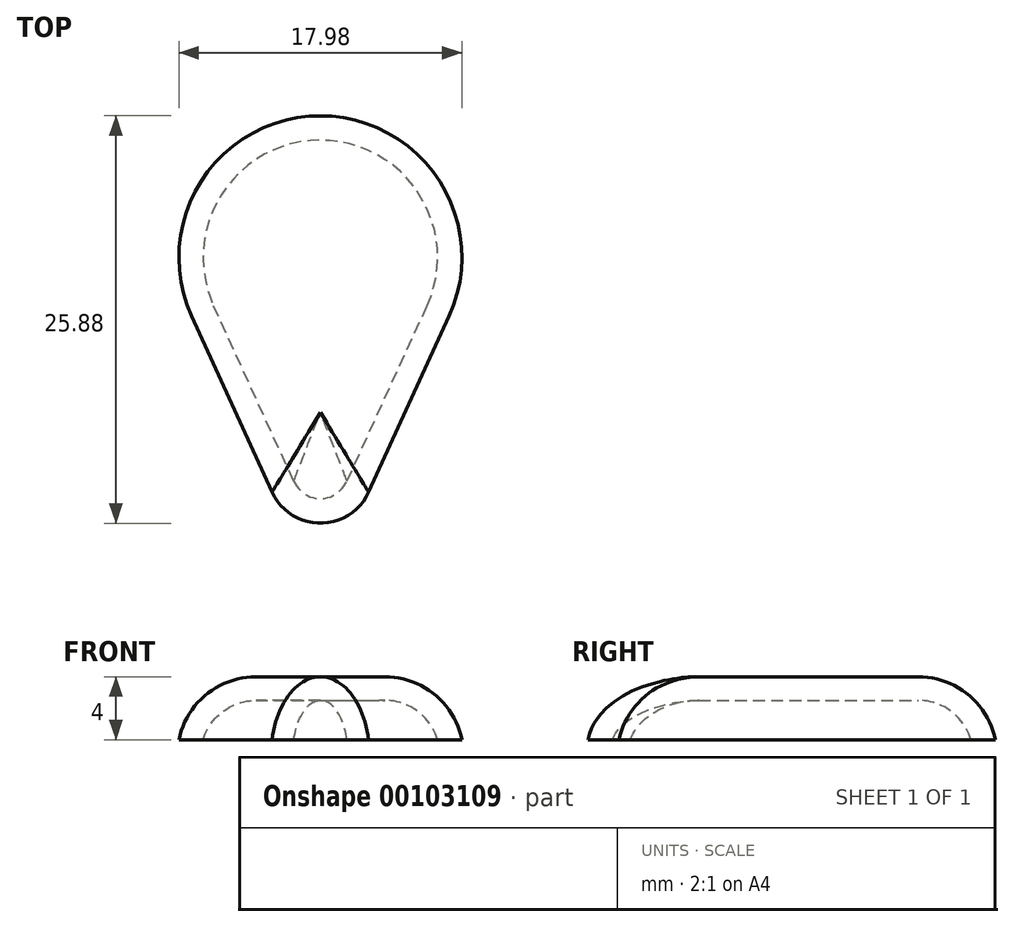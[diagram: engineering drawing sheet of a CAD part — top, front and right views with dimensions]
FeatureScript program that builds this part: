
annotation { "Feature Type Name" : "Feature", "Feature Type Description" : "" }
export const myFeature = defineFeature(function(context is Context, id is Id, definition is map)
    precondition{}
    {
        {
            var Q0;
            Q0=qCreatedBy(makeId("Top.planeOp"),FACE);
            var sketch = newSketch(context, id + "F0", { "sketchPlane" : qUnion([Q0])});
            skLineSegment(sketch, "E0", {"start": v(-3.07, -8.68) * mm, "end": v(-8.18, 2.5) * mm});
            skLineSegment(sketch, "E1.MirrorCS", {"start": v(3.07, -8.68) * mm, "end": v(8.18, 2.5) * mm});
            skArc(sketch, "E2", {"start": v(-3.07, -8.68) * mm, "mid": v(0, -10.65) * mm, "end": v(3.07, -8.68) * mm});
            skArc(sketch, "E3", {"start": v(8.18, 2.5) * mm, "mid": v(0, 15.23) * mm, "end": v(-8.18, 2.5) * mm});
            skSolve(sketch);
        }
        {
            var Q0;
            Q0=makeQuery(id+"F0.imprint","IMPRINT",FACE,{"disambiguationData":[TD([[makeQuery(id+"F0.imprint","IMPRINT",EDGE,{"derivedFrom":sQuery(id+"F0.wireOp",EDGE,"E0")}),-1.0]])]});
            extrude(context, id + "F1", {"entities" : qUnion([Q0]), "depth" : 4 * mm});
        }
        {
            var Q0;
            Q0=makeQuery(id+"F1.opExtrude","CAP_EDGE",EDGE,{"disambiguationData":[OSD([sQuery(id+"F0.wireOp",EDGE,"E0")])],"isStart":false});
            fillet(context, id + "F2", {"entities" : qUnion([Q0]), "radius" : 5 * mm, "tangentPropagation" : true, "allowEdgeOverflow" : false});
        }
        {
            var Q0;
            Q0=makeQuery(id+"F1.opExtrude","CAP_FACE",FACE,{"disambiguationData":[OSD([sQuery(id+"F0.wireOp",EDGE,"E0"),sQuery(id+"F0.wireOp",EDGE,"E1.MirrorCS"),sQuery(id+"F0.wireOp",EDGE,"E2"),sQuery(id+"F0.wireOp",EDGE,"E3")])],"isStart":true});
            shell(context, id + "F3", {"entities" : qUnion([Q0]), "thickness" : 1.5 * mm});
        }
    });
